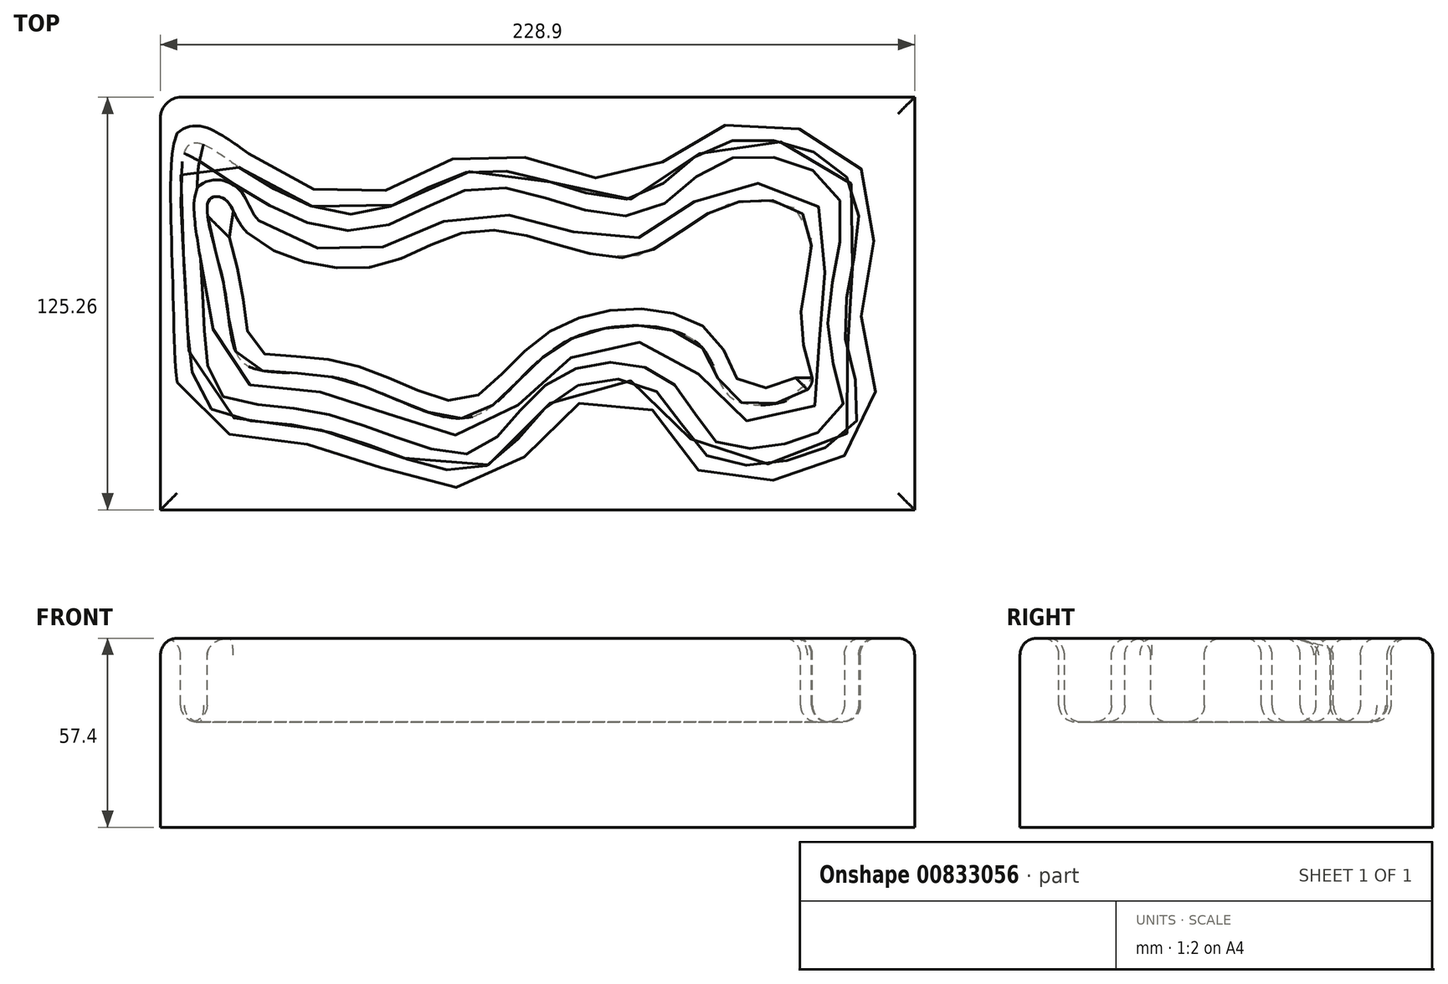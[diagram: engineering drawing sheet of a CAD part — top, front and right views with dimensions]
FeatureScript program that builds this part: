
annotation { "Feature Type Name" : "Feature", "Feature Type Description" : "" }
export const myFeature = defineFeature(function(context is Context, id is Id, definition is map)
    precondition{}
    {
        {
            var Q0;
            Q0=qCreatedBy(makeId("Top.planeOp"),FACE);
            var sketch = newSketch(context, id + "F0", { "sketchPlane" : qUnion([Q0])});
            skLineSegment(sketch, "E0.bottom", {"start": v(-114.45, -62.63) * mm, "end": v(114.45, -62.63) * mm});
            skLineSegment(sketch, "E0.top", {"start": v(-108.1, 62.63) * mm, "end": v(114.45, 62.63) * mm});
            skLineSegment(sketch, "E0.left", {"start": v(-114.45, -62.63) * mm, "end": v(-114.45, 56.28) * mm});
            skLineSegment(sketch, "E0.right", {"start": v(114.45, -62.63) * mm, "end": v(114.45, 62.63) * mm});
            skPoint(sketch, "E0.middle", {"position": v(0, 0) * mm});
            skPoint(sketch, "E1.visualSharp", {"position": v(-114.45, 62.63) * mm});
            skArc(sketch, "E1.filletArc", {"start": v(-108.1, 62.63) * mm, "mid": v(-112.59, 60.77) * mm, "end": v(-114.45, 56.28) * mm});
            skSolve(sketch);
        }
        {
            var Q0;
            Q0=makeQuery(id+"F0.imprint","IMPRINT",FACE,{"disambiguationData":[TD([[makeQuery(id+"F0.imprint","IMPRINT",EDGE,{"derivedFrom":sQuery(id+"F0.wireOp",EDGE,"E0.bottom")}),1.0]])]});
            extrude(context, id + "F1", {"entities" : qUnion([Q0]), "endBound" : BoundingType.SYMMETRIC, "depth" : 57.4 * mm, "offsetDistance" : 25.4 * mm});
        }
        {
            var Q0;
            Q0=makeQuery(id+"F1.opExtrude","CAP_FACE",FACE,{"disambiguationData":[OSD([sQuery(id+"F0.wireOp",EDGE,"E0.bottom"),sQuery(id+"F0.wireOp",EDGE,"E0.top"),sQuery(id+"F0.wireOp",EDGE,"E0.left"),sQuery(id+"F0.wireOp",EDGE,"E0.right"),sQuery(id+"F0.wireOp",EDGE,"E1.filletArc")])],"isStart":false});
            var sketch = newSketch(context, id + "F2", { "sketchPlane" : qUnion([Q0])});
            skFitSpline(sketch, "E2", {"points": [v(-90.53, 41.38) * mm, v(-52.57, 27.33) * mm, v(-16.13, 40.62) * mm, v(29.42, 31.89) * mm, v(54.47, 48.2) * mm, v(95.09, 36.44) * mm, v(93.2, -8.73) * mm, v(96.23, -36.82) * mm, v(53.71, -47.45) * mm, v(37.4, -27.71) * mm, v(8.16, -26.95) * mm, v(-17.65, -50.1) * mm, v(-65.86, -38.34) * mm, v(-99.64, -31.5) * mm, v(-106.86, 4.56) * mm, v(-105.72, 48.2) * mm, v(-90.53, 41.38) * mm]});
            skFitSpline(sketch, "E3", {"points": [v(-88.26, 21.64) * mm, v(-51.06, 11) * mm, v(-16.13, 22.4) * mm, v(27.9, 14.05) * mm, v(55.61, 29.23) * mm, v(81.8, 25.43) * mm, v(79.9, -7.97) * mm, v(82.56, -25.43) * mm, v(59.79, -29.23) * mm, v(49.16, -12.53) * mm, v(8.16, -11.77) * mm, v(-20.69, -34.54) * mm, v(-60.17, -22.78) * mm, v(-89.02, -18.22) * mm, v(-95.09, 4.93) * mm, v(-99.64, 31.5) * mm, v(-94.7, 31.5) * mm, v(-88.26, 21.64) * mm]});
            skSolve(sketch);
        }
        {
            var Q0;
            Q0=makeQuery(id+"F2.imprint","IMPRINT",FACE,{"disambiguationData":[TD([[makeQuery(id+"F2.imprint","IMPRINT",EDGE,{"derivedFrom":sQuery(id+"F2.wireOp",EDGE,"E2")}),-1.0]])]});
            extrude(context, id + "F3", {"entities" : qUnion([Q0]), "operationType" : NewBodyOperationType.REMOVE, "oppositeDirection" : true, "depth" : 25.4 * mm, "offsetDistance" : 25.4 * mm});
        }
        {
            var Q0;
            Q0=makeQuery(id+"F3.boolean.opBoolean","SPLIT",FACE,{"disambiguationData":[TD([makeQuery(id+"F3.opExtrude","SWEPT_FACE",FACE,{"disambiguationData":[OSD([sQuery(id+"F2.wireOp",EDGE,"E3")])]})])],"derivedFrom":makeQuery(id+"F1.opExtrude","CAP_FACE",FACE,{"disambiguationData":[OSD([sQuery(id+"F0.wireOp",EDGE,"E0.bottom"),sQuery(id+"F0.wireOp",EDGE,"E0.top"),sQuery(id+"F0.wireOp",EDGE,"E0.left"),sQuery(id+"F0.wireOp",EDGE,"E0.right"),sQuery(id+"F0.wireOp",EDGE,"E1.filletArc")])],"isStart":false})});
            var Q1;
            {var subQ0=sQuery(id+"F0.wireOp",EDGE,"E0.left");var subQ1=sQuery(id+"F0.wireOp",EDGE,"E0.top");var subQ2=sQuery(id+"F0.wireOp",EDGE,"E0.right");var subQ3=sQuery(id+"F0.wireOp",EDGE,"E0.bottom");var subQ4=sQuery(id+"F0.wireOp",EDGE,"E1.filletArc");Q1=makeQuery(id+"F3.boolean.opBoolean","SPLIT",FACE,{"disambiguationData":[TD([makeQuery(id+"F1.opExtrude","SWEPT_FACE",FACE,{"disambiguationData":[OSD([subQ3])]})])],"derivedFrom":makeQuery(id+"F1.opExtrude","CAP_FACE",FACE,{"disambiguationData":[OSD([subQ3,subQ1,subQ0,subQ2,subQ4])],"isStart":false})});}
            var Q2;
            Q2=makeQuery(id+"F3.boolean.opBoolean","COPY",FACE,{"derivedFrom":makeQuery(id+"F3.opExtrude","CAP_FACE",FACE,{"disambiguationData":[OSD([sQuery(id+"F2.wireOp",EDGE,"E2"),sQuery(id+"F2.wireOp",EDGE,"E3")])],"isStart":false})});
            fillet(context, id + "F4", {"entities" : qUnion([Q0, Q1, Q2]), "radius" : 5.08 * mm, "tangentPropagation" : true, "allowEdgeOverflow" : false});
        }
    });
